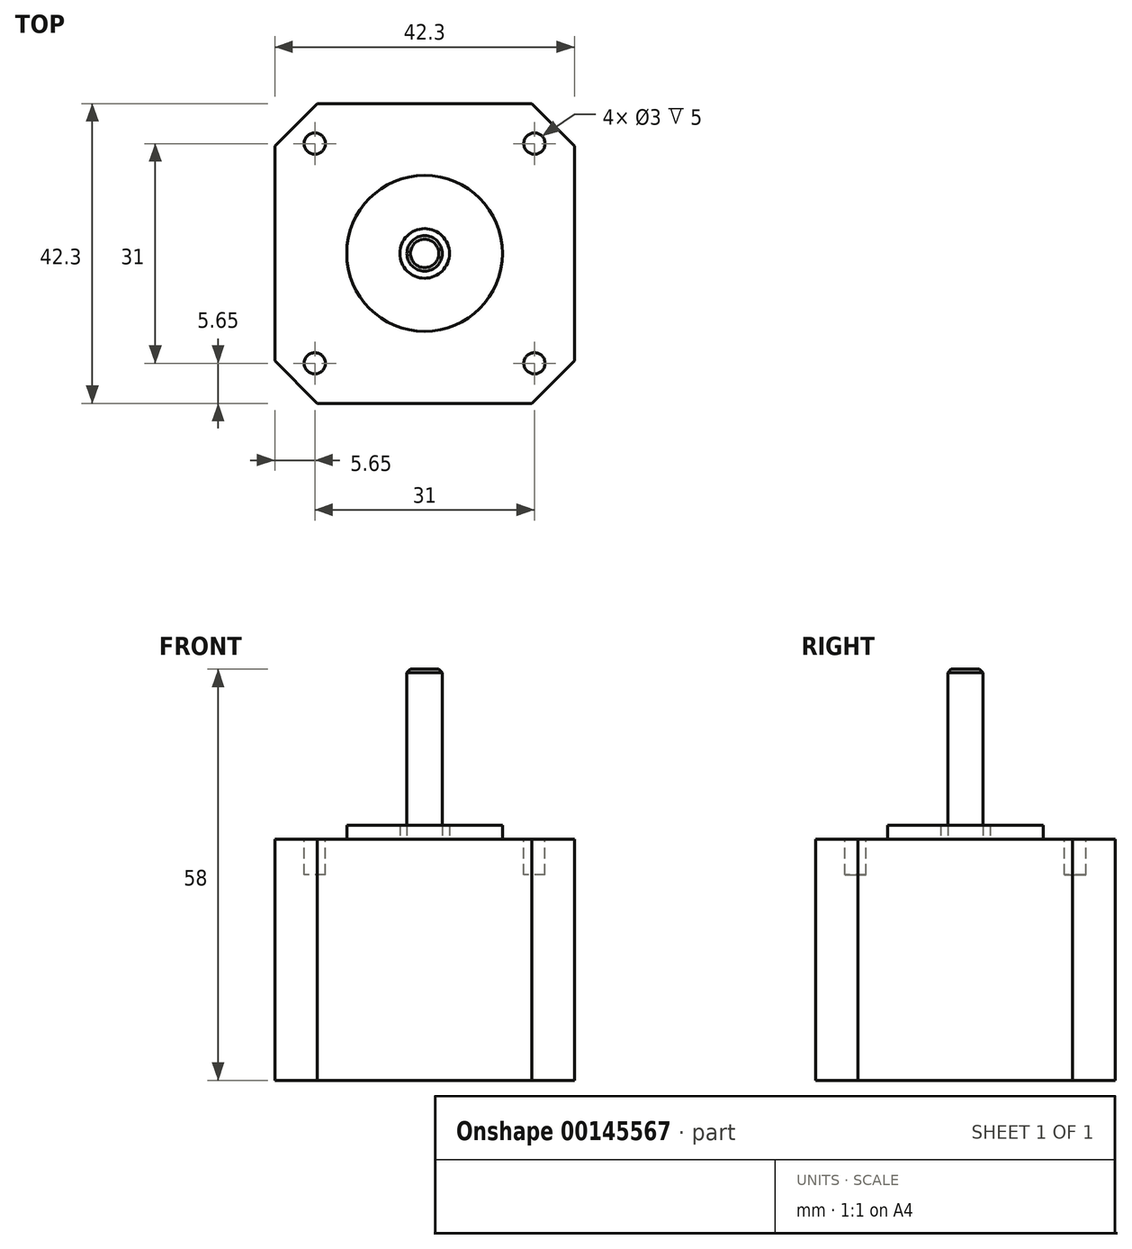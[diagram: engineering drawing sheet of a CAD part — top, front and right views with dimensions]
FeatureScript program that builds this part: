
annotation { "Feature Type Name" : "Feature", "Feature Type Description" : "" }
export const myFeature = defineFeature(function(context is Context, id is Id, definition is map)
    precondition{}
    {
        {
            var Q0;
            Q0=qCreatedBy(makeId("Top.planeOp"),FACE);
            var sketch = newSketch(context, id + "F0", { "sketchPlane" : qUnion([Q0])});
            skLineSegment(sketch, "E0.bottom", {"start": v(21.15, -21.15) * mm, "end": v(-21.15, -21.15) * mm});
            skLineSegment(sketch, "E0.top", {"start": v(21.15, 21.15) * mm, "end": v(-21.15, 21.15) * mm});
            skLineSegment(sketch, "E0.left", {"start": v(21.15, -21.15) * mm, "end": v(21.15, 21.15) * mm});
            skLineSegment(sketch, "E0.right", {"start": v(-21.15, -21.15) * mm, "end": v(-21.15, 21.15) * mm});
            skPoint(sketch, "E0.middle", {"position": v(0, 0) * mm});
            skSolve(sketch);
        }
        {
            var Q0;
            Q0 = qSketchRegion(id + "F0", true);
            extrude(context, id + "F1", {"entities" : qUnion([Q0]), "depth" : 34 * mm});
        }
        {
            var Q0;
            Q0=makeQuery(id+"F1.opExtrude","CAP_FACE",FACE,{"disambiguationData":[OSD([sQuery(id+"F0.wireOp",EDGE,"E0.bottom"),sQuery(id+"F0.wireOp",EDGE,"E0.top"),sQuery(id+"F0.wireOp",EDGE,"E0.left"),sQuery(id+"F0.wireOp",EDGE,"E0.right")])],"isStart":false});
            var sketch = newSketch(context, id + "F2", { "sketchPlane" : qUnion([Q0])});
            skCircle(sketch, "E1", {"center": v(0, 0) * mm, "radius": 11 * mm});
            skCircle(sketch, "E2", {"center": v(0, 0) * mm, "radius": 3.5 * mm});
            skSolve(sketch);
        }
        {
            var Q0;
            Q0 = qSketchRegion(id + "F2", true);
            extrude(context, id + "F3", {"entities" : qUnion([Q0]), "operationType" : NewBodyOperationType.ADD, "depth" : 2 * mm});
        }
        {
            var Q0;
            Q0=makeQuery(id+"F3.boolean.opBoolean","SPLIT",FACE,{"disambiguationData":[TD([makeQuery(id+"F3.opExtrude","SWEPT_FACE",FACE,{"disambiguationData":[OSD([sQuery(id+"F2.wireOp",EDGE,"E2")])]})])],"derivedFrom":makeQuery(id+"F1.opExtrude","CAP_FACE",FACE,{"disambiguationData":[OSD([sQuery(id+"F0.wireOp",EDGE,"E0.bottom"),sQuery(id+"F0.wireOp",EDGE,"E0.top"),sQuery(id+"F0.wireOp",EDGE,"E0.left"),sQuery(id+"F0.wireOp",EDGE,"E0.right")])],"isStart":false})});
            var sketch = newSketch(context, id + "F4", { "sketchPlane" : qUnion([Q0])});
            skCircle(sketch, "E3", {"center": v(0, 0) * mm, "radius": 2.5 * mm});
            skSolve(sketch);
        }
        {
            var Q0;
            Q0 = qSketchRegion(id + "F4", true);
            extrude(context, id + "F5", {"entities" : qUnion([Q0]), "operationType" : NewBodyOperationType.ADD, "depth" : 24 * mm});
        }
        {
            var Q0;
            Q0=makeQuery(id+"F5.opExtrude","CAP_EDGE",EDGE,{"disambiguationData":[OSD([sQuery(id+"F4.wireOp",EDGE,"E3")])],"isStart":false});
            chamfer(context, id + "F6", {"entities" : qUnion([Q0]), "width" : 0.5 * mm, "tangentPropagation" : true});
        }
        {
            var Q0;
            {var subQ0=sQuery(id+"F0.wireOp",EDGE,"E0.right");var subQ1=sQuery(id+"F0.wireOp",EDGE,"E0.left");var subQ2=sQuery(id+"F0.wireOp",EDGE,"E0.top");var subQ3=sQuery(id+"F0.wireOp",EDGE,"E0.bottom");Q0=makeQuery(id+"F3.boolean.opBoolean","SPLIT",FACE,{"disambiguationData":[TD([makeQuery(id+"F1.opExtrude","SWEPT_FACE",FACE,{"disambiguationData":[OSD([subQ3])]})])],"derivedFrom":makeQuery(id+"F1.opExtrude","CAP_FACE",FACE,{"disambiguationData":[OSD([subQ3,subQ2,subQ1,subQ0])],"isStart":false})});}
            var sketch = newSketch(context, id + "F7", { "sketchPlane" : qUnion([Q0])});
            skCircle(sketch, "E4", {"center": v(-15.5, 15.5) * mm, "radius": 1.5 * mm});
            skCircle(sketch, "E5.0.1.0", {"center": v(-15.5, -15.5) * mm, "radius": 1.5 * mm});
            skCircle(sketch, "E5.1.0.0", {"center": v(15.5, 15.5) * mm, "radius": 1.5 * mm});
            skCircle(sketch, "E5.1.1.0", {"center": v(15.5, -15.5) * mm, "radius": 1.5 * mm});
            skLineSegment(sketch, "E5.direction1", {"start": v(-15.5, 15.5) * mm, "end": v(15.5, 15.5) * mm, "construction": true});
            skLineSegment(sketch, "E5.direction2", {"start": v(-15.5, 15.5) * mm, "end": v(-15.5, -15.5) * mm, "construction": true});
            skSolve(sketch);
        }
        {
            var Q0;
            Q0 = qSketchRegion(id + "F7", true);
            extrude(context, id + "F8", {"entities" : qUnion([Q0]), "operationType" : NewBodyOperationType.REMOVE, "oppositeDirection" : true, "depth" : 5 * mm});
        }
        {
            var Q0;
            Q0=makeQuery(id+"F1.opExtrude","SWEPT_EDGE",EDGE,{"disambiguationData":[OSD([sQuery(id+"F0.wireOp",EDGE,"E0.bottom"),sQuery(id+"F0.wireOp",EDGE,"E0.left")])]});
            var Q1;
            Q1=makeQuery(id+"F1.opExtrude","SWEPT_EDGE",EDGE,{"disambiguationData":[OSD([sQuery(id+"F0.wireOp",EDGE,"E0.bottom"),sQuery(id+"F0.wireOp",EDGE,"E0.right")])]});
            var Q2;
            Q2=makeQuery(id+"F1.opExtrude","SWEPT_EDGE",EDGE,{"disambiguationData":[OSD([sQuery(id+"F0.wireOp",EDGE,"E0.top"),sQuery(id+"F0.wireOp",EDGE,"E0.left")])]});
            var Q3;
            Q3=makeQuery(id+"F1.opExtrude","SWEPT_EDGE",EDGE,{"disambiguationData":[OSD([sQuery(id+"F0.wireOp",EDGE,"E0.top"),sQuery(id+"F0.wireOp",EDGE,"E0.right")])]});
            chamfer(context, id + "F9", {"entities" : qUnion([Q0, Q1, Q2, Q3]), "width" : 6 * mm, "tangentPropagation" : true});
        }
    });
